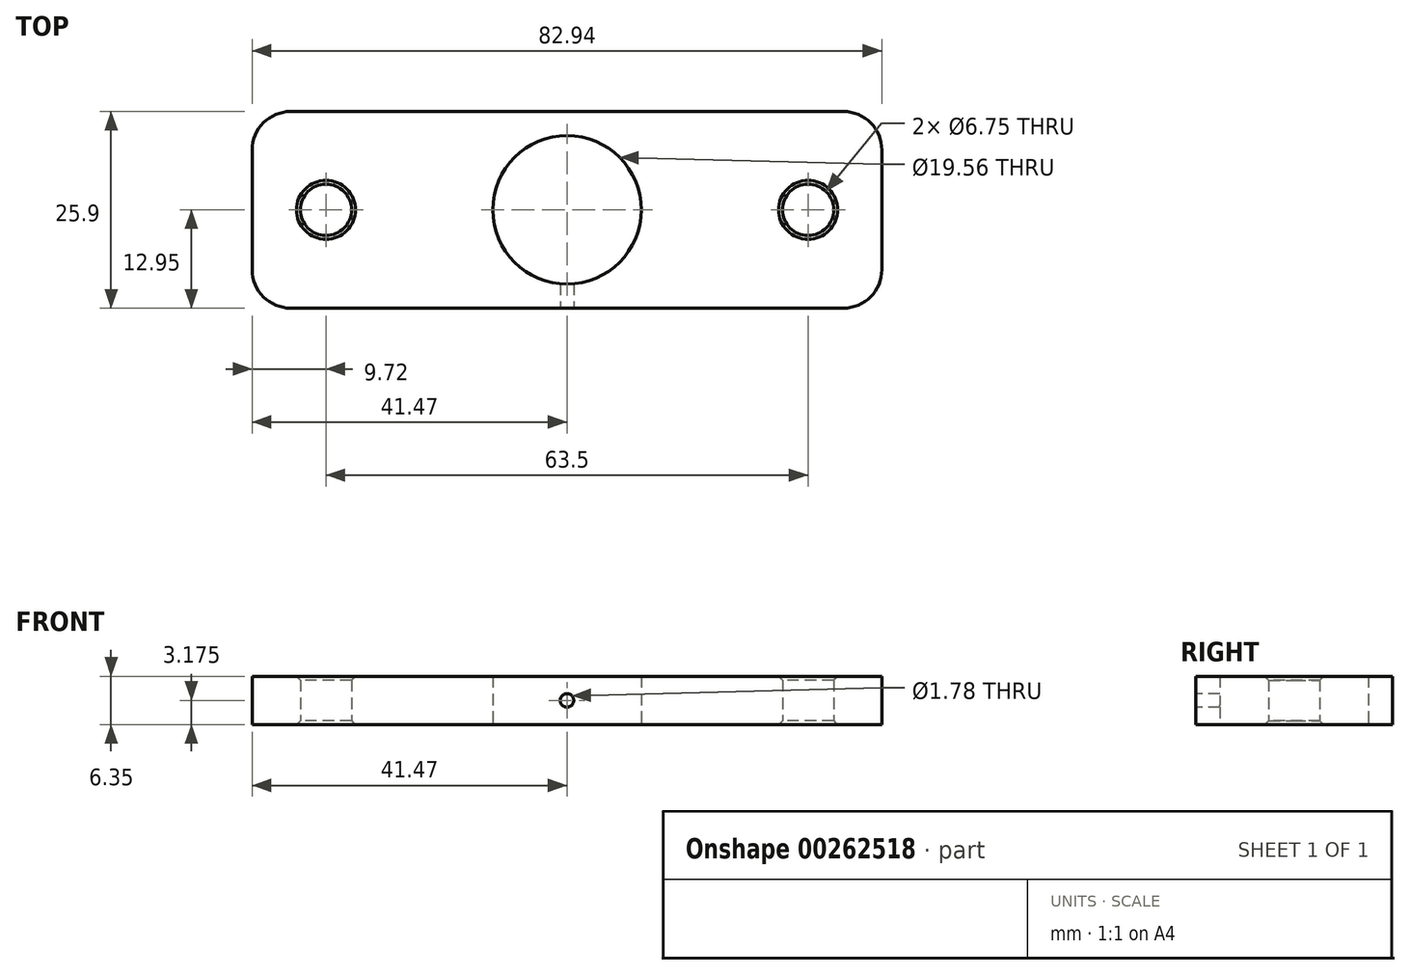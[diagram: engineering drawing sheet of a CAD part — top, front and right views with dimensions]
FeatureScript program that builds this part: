
annotation { "Feature Type Name" : "Feature", "Feature Type Description" : "" }
export const myFeature = defineFeature(function(context is Context, id is Id, definition is map)
    precondition{}
    {
        {
            var Q0;
            Q0=qCreatedBy(makeId("Top.planeOp"),FACE);
            var sketch = newSketch(context, id + "F0", { "sketchPlane" : qUnion([Q0])});
            skLineSegment(sketch, "E0.bottom", {"start": v(41.47, -12.95) * mm, "end": v(-41.47, -12.95) * mm});
            skLineSegment(sketch, "E0.top", {"start": v(41.47, 12.95) * mm, "end": v(-41.47, 12.95) * mm});
            skLineSegment(sketch, "E0.left", {"start": v(41.47, -12.95) * mm, "end": v(41.47, 12.95) * mm});
            skLineSegment(sketch, "E0.right", {"start": v(-41.47, -12.95) * mm, "end": v(-41.47, 12.95) * mm});
            skPoint(sketch, "E0.middle", {"position": v(0, 0) * mm});
            skCircle(sketch, "E1", {"center": v(0, 0) * mm, "radius": 9.78 * mm});
            skCircle(sketch, "E2", {"center": v(-31.75, 0) * mm, "radius": 3.37 * mm});
            skCircle(sketch, "E3.MirrorC", {"center": v(31.75, 0) * mm, "radius": 3.37 * mm});
            skSolve(sketch);
        }
        {
            var Q0;
            Q0 = qSketchRegion(id + "F0", true);
            extrude(context, id + "F1", {"entities" : qUnion([Q0]), "depth" : 6.35 * mm});
        }
        {
            var Q0;
            Q0=makeQuery(id+"F1.opExtrude","SWEPT_FACE",FACE,{"disambiguationData":[OSD([sQuery(id+"F0.wireOp",EDGE,"E0.bottom")])]});
            var sketch = newSketch(context, id + "F2", { "sketchPlane" : qUnion([Q0])});
            skCircle(sketch, "E4", {"center": v(0, 3.18) * mm, "radius": 0.89 * mm});
            skPoint(sketch, "E4.centerSnap0", {"position": v(0, 0) * mm});
            skLineSegment(sketch, "E5", {"start": v(0, 3.18) * mm, "end": v(0, 6.35) * mm, "construction": true});
            skLineSegment(sketch, "E6", {"start": v(0, 0) * mm, "end": v(0, 3.18) * mm, "construction": true});
            skSolve(sketch);
        }
        {
            var Q0;
            Q0 = qSketchRegion(id + "F2", true);
            extrude(context, id + "F3", {"entities" : qUnion([Q0]), "operationType" : NewBodyOperationType.REMOVE, "endBound" : BoundingType.UP_TO_NEXT, "oppositeDirection" : true, "depth" : 25.4 * mm});
        }
        {
            var Q0;
            Q0=makeQuery(id+"F1.opExtrude","SWEPT_EDGE",EDGE,{"disambiguationData":[OSD([sQuery(id+"F0.wireOp",EDGE,"E0.bottom"),sQuery(id+"F0.wireOp",EDGE,"E0.left")])]});
            var Q1;
            Q1=makeQuery(id+"F1.opExtrude","SWEPT_EDGE",EDGE,{"disambiguationData":[OSD([sQuery(id+"F0.wireOp",EDGE,"E0.top"),sQuery(id+"F0.wireOp",EDGE,"E0.left")])]});
            var Q2;
            Q2=makeQuery(id+"F1.opExtrude","SWEPT_EDGE",EDGE,{"disambiguationData":[OSD([sQuery(id+"F0.wireOp",EDGE,"E0.bottom"),sQuery(id+"F0.wireOp",EDGE,"E0.right")])]});
            var Q3;
            Q3=makeQuery(id+"F1.opExtrude","SWEPT_EDGE",EDGE,{"disambiguationData":[OSD([sQuery(id+"F0.wireOp",EDGE,"E0.top"),sQuery(id+"F0.wireOp",EDGE,"E0.right")])]});
            fillet(context, id + "F4", {"entities" : qUnion([Q0, Q1, Q2, Q3]), "radius" : 5.08 * mm, "tangentPropagation" : true, "allowEdgeOverflow" : false});
        }
        {
            var Q0;
            Q0=makeQuery(id+"F1.opExtrude","CAP_EDGE",EDGE,{"disambiguationData":[OSD([sQuery(id+"F0.wireOp",EDGE,"E2")])],"isStart":false});
            var Q1;
            Q1=makeQuery(id+"F1.opExtrude","CAP_EDGE",EDGE,{"disambiguationData":[OSD([sQuery(id+"F0.wireOp",EDGE,"E3.MirrorC")])],"isStart":false});
            var Q2;
            Q2=makeQuery(id+"F1.opExtrude","CAP_EDGE",EDGE,{"disambiguationData":[OSD([sQuery(id+"F0.wireOp",EDGE,"E2")])],"isStart":true});
            var Q3;
            Q3=makeQuery(id+"F1.opExtrude","CAP_EDGE",EDGE,{"disambiguationData":[OSD([sQuery(id+"F0.wireOp",EDGE,"E3.MirrorC")])],"isStart":true});
            chamfer(context, id + "F5", {"entities" : qUnion([Q0, Q1, Q2, Q3]), "width" : 0.5 * mm, "tangentPropagation" : true});
        }
    });
